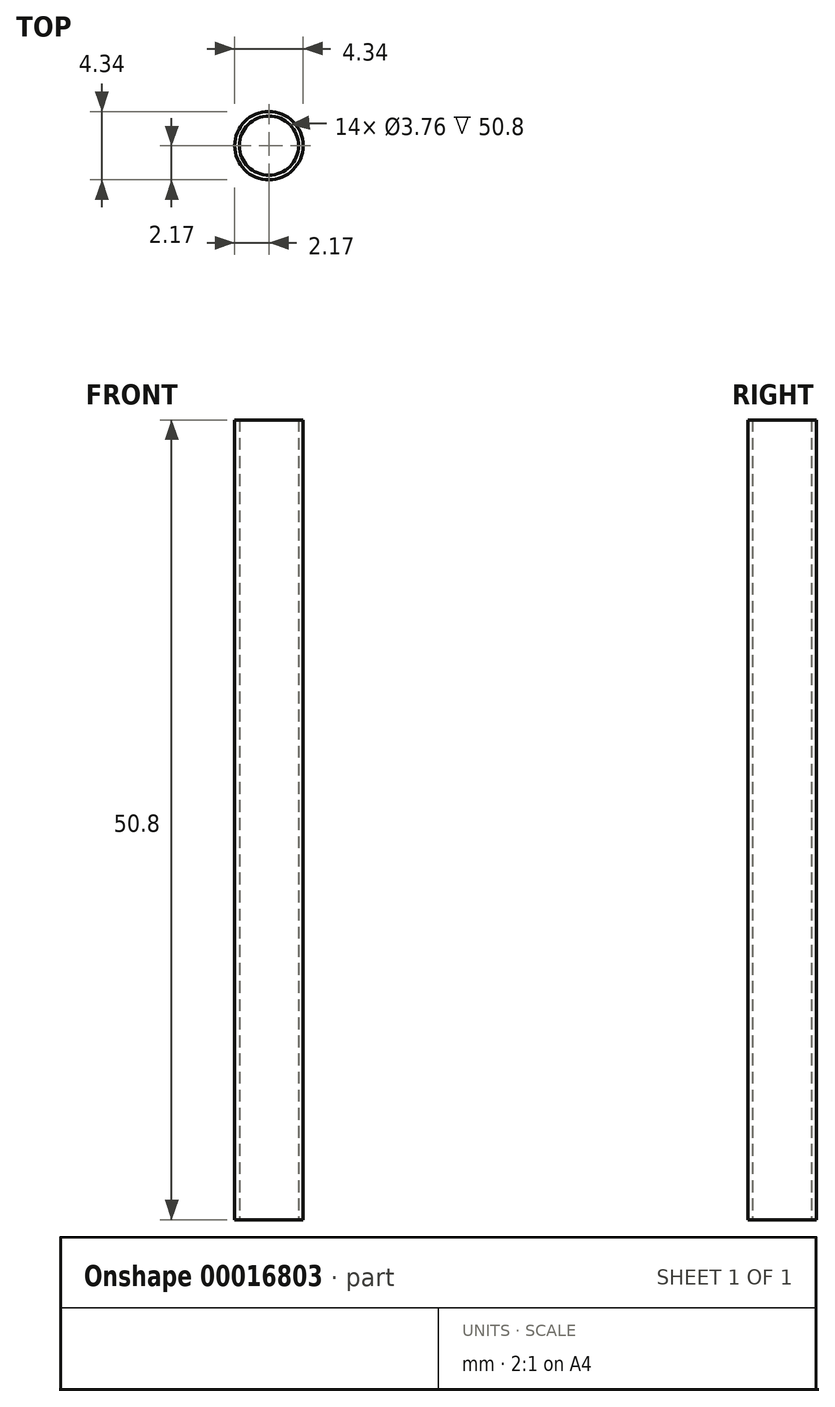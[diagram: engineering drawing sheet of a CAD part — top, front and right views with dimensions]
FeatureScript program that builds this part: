
annotation { "Feature Type Name" : "Feature", "Feature Type Description" : "" }
export const myFeature = defineFeature(function(context is Context, id is Id, definition is map)
    precondition{}
    {
        {
            var Q0;
            Q0=qCreatedBy(makeId("Front.planeOp"),FACE);
            var sketch = newSketch(context, id + "F0", { "sketchPlane" : qUnion([Q0])});
            skLineSegment(sketch, "E0", {"start": v(0, 0) * mm, "end": v(1.88, 0) * mm});
            skLineSegment(sketch, "E1", {"start": v(1.88, 0) * mm, "end": v(1.88, 50.8) * mm});
            skLineSegment(sketch, "E2", {"start": v(1.88, 50.8) * mm, "end": v(2.17, 50.8) * mm});
            skLineSegment(sketch, "E3", {"start": v(2.17, 50.8) * mm, "end": v(2.17, 0) * mm});
            skLineSegment(sketch, "E4", {"start": v(2.17, 0) * mm, "end": v(1.88, 0) * mm});
            skLineSegment(sketch, "E5", {"start": v(0, 0) * mm, "end": v(0, 50.8) * mm});
            skLineSegment(sketch, "E6", {"start": v(0, 50.8) * mm, "end": v(1.88, 50.8) * mm});
            skSolve(sketch);
        }
        {
            var Q0;
            Q0=makeQuery(id+"F0.imprint","IMPRINT",FACE,{"disambiguationData":[TD([[makeQuery(id+"F0.imprint","IMPRINT",EDGE,{"derivedFrom":sQuery(id+"F0.wireOp",EDGE,"E1")}),-1.0]])]});
            var Q1;
            Q1=sQuery(id+"F0.wireOp",EDGE,"E5");
            revolve(context, id + "F1", {"entities" : qUnion([Q0]), "axis" : qUnion([Q1]), "revolveType" : RevolveType.FULL});
        }
    });
